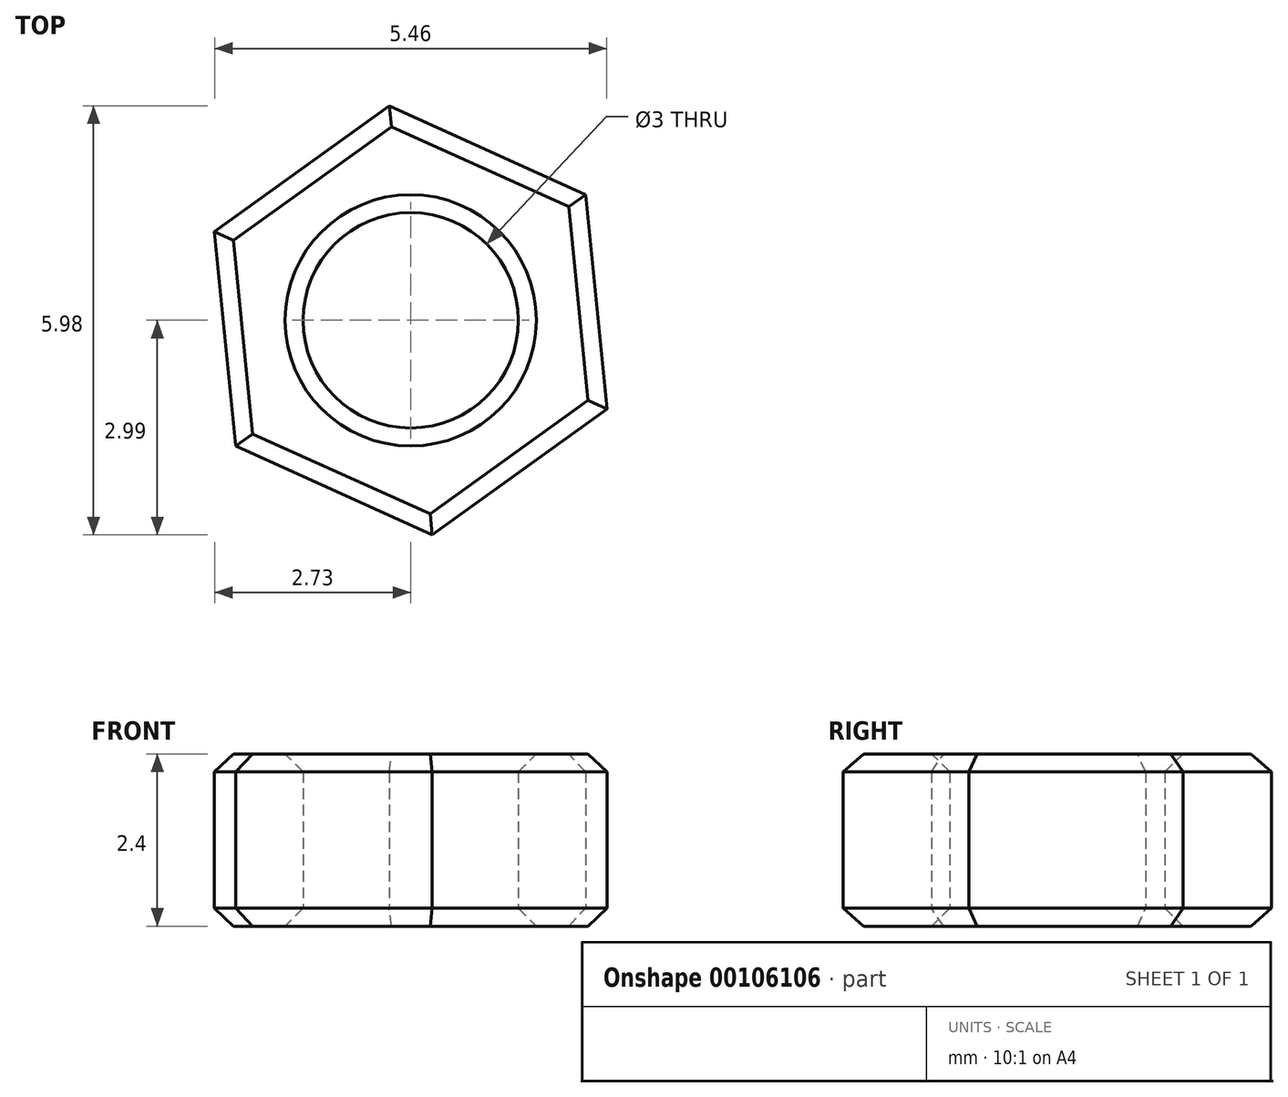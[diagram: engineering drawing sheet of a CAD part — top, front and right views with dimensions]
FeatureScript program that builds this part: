
annotation { "Feature Type Name" : "Feature", "Feature Type Description" : "" }
export const myFeature = defineFeature(function(context is Context, id is Id, definition is map)
    precondition{}
    {
        {
            var Q0;
            Q0=qCreatedBy(makeId("Top.planeOp"),FACE);
            var sketch = newSketch(context, id + "F0", { "sketchPlane" : qUnion([Q0])});
            skCircle(sketch, "E0.cCircle", {"center": v(0, 0) * mm, "radius": 2.6 * mm, "construction": true});
            skLineSegment(sketch, "E0.0", {"start": v(2.73, -1.23) * mm, "end": v(0.3, -2.99) * mm});
            skLineSegment(sketch, "E0.1", {"start": v(0.3, -2.99) * mm, "end": v(-2.44, -1.75) * mm});
            skLineSegment(sketch, "E0.2", {"start": v(-2.44, -1.75) * mm, "end": v(-2.73, 1.23) * mm});
            skLineSegment(sketch, "E0.3", {"start": v(-2.73, 1.23) * mm, "end": v(-0.3, 2.99) * mm});
            skLineSegment(sketch, "E0.4", {"start": v(-0.3, 2.99) * mm, "end": v(2.44, 1.75) * mm});
            skLineSegment(sketch, "E0.5", {"start": v(2.44, 1.75) * mm, "end": v(2.73, -1.23) * mm});
            skPoint(sketch, "E0.0.midPoint", {"position": v(1.52, -2.1) * mm});
            skCircle(sketch, "E1", {"center": v(0, 0) * mm, "radius": 1.5 * mm});
            skSolve(sketch);
        }
        {
            var Q0;
            Q0=makeQuery(id+"F0.imprint","IMPRINT",FACE,{"disambiguationData":[TD([[makeQuery(id+"F0.imprint","IMPRINT",EDGE,{"derivedFrom":sQuery(id+"F0.wireOp",EDGE,"E0.0")}),-1.0]])]});
            extrude(context, id + "F1", {"entities" : qUnion([Q0]), "depth" : 2.4 * mm});
        }
        {
            var Q0;
            Q0=makeQuery(id+"F1.opExtrude","CAP_FACE",FACE,{"disambiguationData":[OSD([sQuery(id+"F0.wireOp",EDGE,"E0.0"),sQuery(id+"F0.wireOp",EDGE,"E0.1"),sQuery(id+"F0.wireOp",EDGE,"E0.2"),sQuery(id+"F0.wireOp",EDGE,"E0.3"),sQuery(id+"F0.wireOp",EDGE,"E0.4"),sQuery(id+"F0.wireOp",EDGE,"E0.5"),sQuery(id+"F0.wireOp",EDGE,"E1")])],"isStart":true});
            chamfer(context, id + "F2", {"entities" : qUnion([Q0]), "width" : .25 * mm, "tangentPropagation" : true});
        }
        {
            var Q0;
            Q0=makeQuery(id+"F1.opExtrude","CAP_FACE",FACE,{"disambiguationData":[OSD([sQuery(id+"F0.wireOp",EDGE,"E0.0"),sQuery(id+"F0.wireOp",EDGE,"E0.1"),sQuery(id+"F0.wireOp",EDGE,"E0.2"),sQuery(id+"F0.wireOp",EDGE,"E0.3"),sQuery(id+"F0.wireOp",EDGE,"E0.4"),sQuery(id+"F0.wireOp",EDGE,"E0.5"),sQuery(id+"F0.wireOp",EDGE,"E1")])],"isStart":false});
            chamfer(context, id + "F3", {"entities" : qUnion([Q0]), "width" : .25 * mm, "tangentPropagation" : true});
        }
    });
